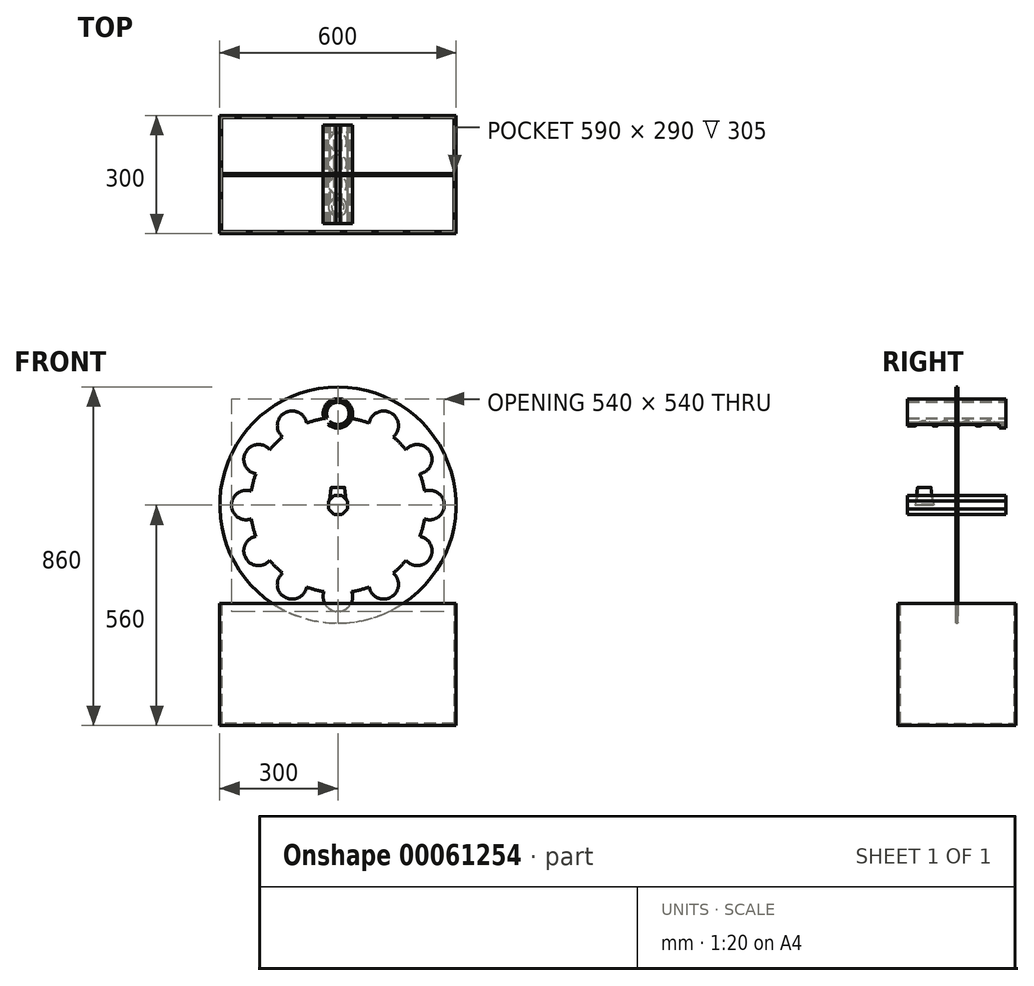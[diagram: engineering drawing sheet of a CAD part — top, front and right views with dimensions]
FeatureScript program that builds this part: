
annotation { "Feature Type Name" : "Feature", "Feature Type Description" : "" }
export const myFeature = defineFeature(function(context is Context, id is Id, definition is map)
    precondition{}
    {
        {
            assignVariable(context, id + "F0", {"name" : "depth", "anyValue" : 250});
        }
        {
            var Q0;
            Q0=qCreatedBy(makeId("Front.planeOp"),FACE);
            var sketch = newSketch(context, id + "F1", { "sketchPlane" : qUnion([Q0])});
            skLineSegment(sketch, "E0.rect.bottom", {"start": v(300, -250) * mm, "end": v(-300, -250) * mm});
            skLineSegment(sketch, "E0.rect.top", {"start": v(300, -560) * mm, "end": v(-300, -560) * mm});
            skLineSegment(sketch, "E0.rect.left", {"start": v(300, -250) * mm, "end": v(300, -560) * mm});
            skLineSegment(sketch, "E0.rect.right", {"start": v(-300, -250) * mm, "end": v(-300, -560) * mm});
            skPoint(sketch, "E0.rect.middle", {"position": v(0, -405) * mm});
            skSolve(sketch);
        }
        {
            var Q0;
            Q0 = qSketchRegion(id + "F1", true);
            extrude(context, id + "F2", {"entities" : qUnion([Q0]), "endBound" : BoundingType.SYMMETRIC, "depth" : 300 * mm});
        }
        {
            var Q0;
            Q0=makeQuery(id+"F2.opExtrude","SWEPT_FACE",FACE,{"disambiguationData":[OSD([sQuery(id+"F1.wireOp",EDGE,"E0.rect.bottom")])]});
            shell(context, id + "F3", {"entities" : qUnion([Q0]), "thickness" : 5 * mm});
        }
        {
            var Q0;
            Q0=qCreatedBy(makeId("Front.planeOp"),FACE);
            var sketch = newSketch(context, id + "F4", { "sketchPlane" : qUnion([Q0])});
            skCircle(sketch, "E1", {"center": v(0, 0) * mm, "radius": 300 * mm});
            skCircle(sketch, "E2", {"center": v(0, 0) * mm, "radius": 232.83 * mm, "construction": true});
            skArc(sketch, "E3", {"start": v(-5, 270) * mm, "mid": v(0, 195.33) * mm, "end": v(5, 270) * mm});
            skCircle(sketch, "E4", {"center": v(0, 232.83) * mm, "radius": 33.9 * mm});
            skCircle(sketch, "E5", {"center": v(0, 232.83) * mm, "radius": 31.5 * mm});
            skCircle(sketch, "E6", {"center": v(0, 232.83) * mm, "radius": 28.5 * mm});
            skCircle(sketch, "E7", {"center": v(0, 0) * mm, "radius": 222.83 * mm});
            skCircle(sketch, "E8.cCircle", {"center": v(0, 0) * mm, "radius": 24.14 * mm, "construction": true});
            skLineSegment(sketch, "E8.0", {"start": v(24.14, 10) * mm, "end": v(24.14, -10) * mm});
            skLineSegment(sketch, "E8.1", {"start": v(24.14, -10) * mm, "end": v(10, -24.14) * mm});
            skLineSegment(sketch, "E8.2", {"start": v(10, -24.14) * mm, "end": v(-10, -24.14) * mm});
            skLineSegment(sketch, "E8.3", {"start": v(-10, -24.14) * mm, "end": v(-24.14, -10) * mm});
            skLineSegment(sketch, "E8.4", {"start": v(-24.14, -10) * mm, "end": v(-24.14, 10) * mm});
            skLineSegment(sketch, "E8.5", {"start": v(-24.14, 10) * mm, "end": v(-10, 24.14) * mm});
            skLineSegment(sketch, "E8.6", {"start": v(-10, 24.14) * mm, "end": v(10, 24.14) * mm});
            skLineSegment(sketch, "E8.7", {"start": v(10, 24.14) * mm, "end": v(24.14, 10) * mm});
            skPoint(sketch, "E8.0.midPoint", {"position": v(24.14, 0) * mm});
            skLineSegment(sketch, "E9", {"start": v(0, 232.83) * mm, "end": v(-25, 204.88) * mm});
            skLineSegment(sketch, "E10", {"start": v(0, 232.83) * mm, "end": v(25, 204.88) * mm});
            skLineSegment(sketch, "E11", {"start": v(-25, 204.88) * mm, "end": v(25, 204.88) * mm, "construction": true});
            skLineSegment(sketch, "E12", {"start": v(-5, 270) * mm, "end": v(5, 270) * mm});
            skArc(sketch, "E13.1.0", {"start": v(-139.33, 231.33) * mm, "mid": v(-97.67, 169.16) * mm, "end": v(-130.67, 236.33) * mm});
            skLineSegment(sketch, "E13.1.1", {"start": v(-139.33, 231.33) * mm, "end": v(-130.67, 236.33) * mm});
            skArc(sketch, "E13.2.0", {"start": v(-236.33, 130.67) * mm, "mid": v(-169.16, 97.67) * mm, "end": v(-231.33, 139.33) * mm});
            skLineSegment(sketch, "E13.2.1", {"start": v(-236.33, 130.67) * mm, "end": v(-231.33, 139.33) * mm});
            skArc(sketch, "E14.1.3.0", {"start": v(-270, -5) * mm, "mid": v(-195.33, 0) * mm, "end": v(-270, 5) * mm});
            skLineSegment(sketch, "E14.4.3.0", {"start": v(-270, -5) * mm, "end": v(-270, 5) * mm});
            skArc(sketch, "E14.1.4.0", {"start": v(-231.33, -139.33) * mm, "mid": v(-169.16, -97.67) * mm, "end": v(-236.33, -130.67) * mm});
            skLineSegment(sketch, "E14.4.4.0", {"start": v(-231.33, -139.33) * mm, "end": v(-236.33, -130.67) * mm});
            skArc(sketch, "E14.1.5.0", {"start": v(-130.67, -236.33) * mm, "mid": v(-97.67, -169.16) * mm, "end": v(-139.33, -231.33) * mm});
            skLineSegment(sketch, "E14.4.5.0", {"start": v(-130.67, -236.33) * mm, "end": v(-139.33, -231.33) * mm});
            skArc(sketch, "E14.1.6.0", {"start": v(5, -270) * mm, "mid": v(0, -195.33) * mm, "end": v(-5, -270) * mm});
            skLineSegment(sketch, "E14.4.6.0", {"start": v(5, -270) * mm, "end": v(-5, -270) * mm});
            skArc(sketch, "E14.1.7.0", {"start": v(139.33, -231.33) * mm, "mid": v(97.67, -169.16) * mm, "end": v(130.67, -236.33) * mm});
            skLineSegment(sketch, "E14.4.7.0", {"start": v(139.33, -231.33) * mm, "end": v(130.67, -236.33) * mm});
            skArc(sketch, "E14.1.8.0", {"start": v(236.33, -130.67) * mm, "mid": v(169.16, -97.67) * mm, "end": v(231.33, -139.33) * mm});
            skLineSegment(sketch, "E14.4.8.0", {"start": v(236.33, -130.67) * mm, "end": v(231.33, -139.33) * mm});
            skArc(sketch, "E14.1.9.0", {"start": v(270, 5) * mm, "mid": v(195.33, 0) * mm, "end": v(270, -5) * mm});
            skLineSegment(sketch, "E14.4.9.0", {"start": v(270, 5) * mm, "end": v(270, -5) * mm});
            skArc(sketch, "E14.1.10.0", {"start": v(231.33, 139.33) * mm, "mid": v(169.16, 97.67) * mm, "end": v(236.33, 130.67) * mm});
            skLineSegment(sketch, "E14.4.10.0", {"start": v(231.33, 139.33) * mm, "end": v(236.33, 130.67) * mm});
            skArc(sketch, "E14.1.11.0", {"start": v(130.67, 236.33) * mm, "mid": v(97.67, 169.16) * mm, "end": v(139.33, 231.33) * mm});
            skLineSegment(sketch, "E14.4.11.0", {"start": v(130.67, 236.33) * mm, "end": v(139.33, 231.33) * mm});
            skSolve(sketch);
        }
        {
            var Q0;
            Q0=makeQuery(id+"F4.imprint","IMPRINT",FACE,{"disambiguationData":[TD([[makeQuery(id+"F4.imprint","IMPRINT",EDGE,{"derivedFrom":sQuery(id+"F4.wireOp",EDGE,"E1")}),1.0]])]});
            extrude(context, id + "F5", {"entities" : qUnion([Q0]), "endBound" : BoundingType.SYMMETRIC, "depth" : 5 * mm});
        }
        {
            var Q0;
            {var subQ0=sQuery(id+"F4.wireOp",EDGE,"E7");var subQ1=sQuery(id+"F4.wireOp",EDGE,"E3");var subQ2=makeQuery(id+"F4.imprint","INTERSECT",VERTEX,{"disambiguationData":[OD(0.0)],"derivedFrom":[subQ1,subQ0]});Q0=makeQuery(id+"F4.imprint","IMPRINT",FACE,{"disambiguationData":[TD([[makeQuery(id+"F4.imprint","IMPRINT",EDGE,{"disambiguationData":[TD([[subQ2,-1.0]])],"derivedFrom":subQ1}),1.0]])]});}
            var Q1;
            {var subQ0=sQuery(id+"F4.wireOp",EDGE,"E7");var subQ1=sQuery(id+"F4.wireOp",EDGE,"E3");var subQ2=makeQuery(id+"F4.imprint","INTERSECT",VERTEX,{"disambiguationData":[OD(0.0)],"derivedFrom":[subQ1,subQ0]});Q1=makeQuery(id+"F4.imprint","IMPRINT",FACE,{"disambiguationData":[TD([[makeQuery(id+"F4.imprint","IMPRINT",EDGE,{"disambiguationData":[TD([[subQ2,1.0]])],"derivedFrom":subQ1}),1.0]])]});}
            var Q2;
            {var subQ0=sQuery(id+"F4.wireOp",EDGE,"E10");var subQ1=sQuery(id+"F4.wireOp",EDGE,"E3");var subQ2=makeQuery(id+"F4.imprint","INTERSECT",VERTEX,{"derivedFrom":[subQ1,subQ0]});Q2=makeQuery(id+"F4.imprint","IMPRINT",FACE,{"disambiguationData":[TD([[makeQuery(id+"F4.imprint","IMPRINT",EDGE,{"disambiguationData":[TD([[subQ2,-1.0]])],"derivedFrom":subQ1}),1.0]])]});}
            var Q3;
            {var subQ0=sQuery(id+"F4.wireOp",EDGE,"E9");var subQ1=sQuery(id+"F4.wireOp",EDGE,"E3");var subQ2=makeQuery(id+"F4.imprint","INTERSECT",VERTEX,{"derivedFrom":[subQ1,subQ0]});Q3=makeQuery(id+"F4.imprint","IMPRINT",FACE,{"disambiguationData":[TD([[makeQuery(id+"F4.imprint","IMPRINT",EDGE,{"disambiguationData":[TD([[subQ2,-1.0]])],"derivedFrom":subQ1}),1.0]])]});}
            extrude(context, id + "F6", {"entities" : qUnion([Q0, Q1, Q2, Q3]), "endBound" : BoundingType.SYMMETRIC, "depth" : (getVariable(context, 'depth')) * mm});
        }
        {
            var Q0;
            {var subQ0=sQuery(id+"F4.wireOp",EDGE,"E9");var subQ1=sQuery(id+"F4.wireOp",EDGE,"E3");var subQ2=makeQuery(id+"F4.imprint","INTERSECT",VERTEX,{"derivedFrom":[subQ1,subQ0]});Q0=makeQuery(id+"F4.imprint","IMPRINT",FACE,{"disambiguationData":[TD([[makeQuery(id+"F4.imprint","IMPRINT",EDGE,{"disambiguationData":[TD([[subQ2,-1.0]])],"derivedFrom":subQ1}),1.0]])]});}
            extrude(context, id + "F7", {"entities" : qUnion([Q0]), "operationType" : NewBodyOperationType.REMOVE, "oppositeDirection" : true, "depth" : 107.9 * mm, "hasSecondDirection" : true, "secondDirectionBound" : SecondDirectionBoundingType.THROUGH_ALL, "secondDirectionOppositeDirection" : false, "secondDirectionDepth" : 25 * mm});
        }
        {
            var Q0;
            {var subQ0=sQuery(id+"F4.wireOp",EDGE,"E7");var subQ1=sQuery(id+"F4.wireOp",EDGE,"E5");var subQ2=makeQuery(id+"F4.imprint","INTERSECT",VERTEX,{"disambiguationData":[OD(0.0)],"derivedFrom":[subQ1,subQ0]});Q0=makeQuery(id+"F4.imprint","IMPRINT",FACE,{"disambiguationData":[TD([[makeQuery(id+"F4.imprint","IMPRINT",EDGE,{"disambiguationData":[TD([[subQ2,-1.0]])],"derivedFrom":subQ1}),1.0]])]});}
            var Q1;
            {var subQ0=sQuery(id+"F4.wireOp",EDGE,"E7");var subQ1=sQuery(id+"F4.wireOp",EDGE,"E5");var subQ2=makeQuery(id+"F4.imprint","INTERSECT",VERTEX,{"disambiguationData":[OD(0.0)],"derivedFrom":[subQ1,subQ0]});Q1=makeQuery(id+"F4.imprint","IMPRINT",FACE,{"disambiguationData":[TD([[makeQuery(id+"F4.imprint","IMPRINT",EDGE,{"disambiguationData":[TD([[subQ2,1.0]])],"derivedFrom":subQ1}),1.0]])]});}
            var Q2;
            {var subQ0=sQuery(id+"F4.wireOp",EDGE,"E10");var subQ1=sQuery(id+"F4.wireOp",EDGE,"E5");var subQ2=makeQuery(id+"F4.imprint","INTERSECT",VERTEX,{"derivedFrom":[subQ1,subQ0]});Q2=makeQuery(id+"F4.imprint","IMPRINT",FACE,{"disambiguationData":[TD([[makeQuery(id+"F4.imprint","IMPRINT",EDGE,{"disambiguationData":[TD([[subQ2,-1.0]])],"derivedFrom":subQ1}),1.0]])]});}
            var Q3;
            {var subQ0=sQuery(id+"F4.wireOp",EDGE,"E9");var subQ1=sQuery(id+"F4.wireOp",EDGE,"E5");var subQ2=makeQuery(id+"F4.imprint","INTERSECT",VERTEX,{"derivedFrom":[subQ1,subQ0]});Q3=makeQuery(id+"F4.imprint","IMPRINT",FACE,{"disambiguationData":[TD([[makeQuery(id+"F4.imprint","IMPRINT",EDGE,{"disambiguationData":[TD([[subQ2,-1.0]])],"derivedFrom":subQ1}),1.0]])]});}
            extrude(context, id + "F8", {"entities" : qUnion([Q0, Q1, Q2, Q3]), "endBound" : BoundingType.SYMMETRIC, "depth" : (getVariable(context, 'depth')) * mm});
        }
        {
            var Q0;
            Q0=qCreatedBy(makeId("Top.planeOp"),FACE);
            var sketch = newSketch(context, id + "F9", { "sketchPlane" : qUnion([Q0])});
            skCircle(sketch, "E15", {"center": v(0, -82.5) * mm, "radius": 22.5 * mm});
            skLineSegment(sketch, "E16", {"start": v(0, -82.5) * mm, "end": v(0, 82.5) * mm, "construction": true});
            skCircle(sketch, "E17", {"center": v(0, 82.5) * mm, "radius": 22.5 * mm});
            skCircle(sketch, "E18", {"center": v(0, 27.5) * mm, "radius": 22.5 * mm});
            skCircle(sketch, "E19", {"center": v(0, -27.5) * mm, "radius": 22.5 * mm});
            skLineSegment(sketch, "E20", {"start": v(0, -27.5) * mm, "end": v(0, 27.5) * mm, "construction": true});
            skLineSegment(sketch, "E21", {"start": v(0, 82.5) * mm, "end": v(0, 27.5) * mm, "construction": true});
            skSolve(sketch);
        }
        {
            var Q0;
            Q0 = qSketchRegion(id + "F9", true);
            var Q1;
            Q1=makeQuery(id+"F8.opExtrude","SWEPT_FACE",FACE,{"disambiguationData":[OSD([sQuery(id+"F4.wireOp",EDGE,"E6")])]});
            var Q2;
            Q2=makeQuery(id+"F8.opExtrude","SWEPT_BODY",BODY,{"disambiguationData":[OSD([sQuery(id+"F4.wireOp",EDGE,"E5"),sQuery(id+"F4.wireOp",EDGE,"E6")])]});
            extrude(context, id + "F10", {"entities" : qUnion([Q0]), "operationType" : NewBodyOperationType.REMOVE, "endBound" : BoundingType.UP_TO_SURFACE, "endBoundEntityFace" : qUnion([Q1]), "endBoundEntityBody" : qUnion([Q2]), "depth" : 226.12 * mm});
        }
        {
            var Q0;
            Q0=makeQuery(id+"F4.imprint","IMPRINT",FACE,{"disambiguationData":[TD([[makeQuery(id+"F4.imprint","IMPRINT",EDGE,{"derivedFrom":sQuery(id+"F4.wireOp",EDGE,"E8.0")}),-1.0]])]});
            extrude(context, id + "F11", {"entities" : qUnion([Q0]), "endBound" : BoundingType.SYMMETRIC, "depth" : (getVariable(context, 'depth')) * mm});
        }
        {
            var Q0;
            Q0=qCreatedBy(makeId("Right.planeOp"),FACE);
            var sketch = newSketch(context, id + "F12", { "sketchPlane" : qUnion([Q0])});
            skLineSegment(sketch, "E22.0", {"start": v(-105, 0) * mm, "end": v(-60, 0) * mm, "construction": true});
            skLineSegment(sketch, "E23", {"start": v(-82.5, 43) * mm, "end": v(-82.5, 45) * mm});
            skLineSegment(sketch, "E24", {"start": v(-82.5, 45) * mm, "end": v(-99.72, 45) * mm});
            skLineSegment(sketch, "E25", {"start": v(-99.72, 45) * mm, "end": v(-105, 2) * mm});
            skLineSegment(sketch, "E26", {"start": v(-105, 2) * mm, "end": v(-106.43, 2) * mm});
            skLineSegment(sketch, "E27", {"start": v(-106.43, 2) * mm, "end": v(-106.43, 0) * mm});
            skLineSegment(sketch, "E28", {"start": v(-106.43, 0) * mm, "end": v(-105, 0) * mm});
            skLineSegment(sketch, "E29", {"start": v(-105, 0) * mm, "end": v(-103.43, 0) * mm});
            skLineSegment(sketch, "E30", {"start": v(-103.43, 0) * mm, "end": v(-98.15, 43) * mm});
            skLineSegment(sketch, "E31", {"start": v(-98.15, 43) * mm, "end": v(-82.5, 43) * mm});
            skPoint(sketch, "E32.orphan", {"position": v(-82.5, 0) * mm});
            skSolve(sketch);
        }
        {
            var Q0;
            Q0 = qSketchRegion(id + "F12", true);
            var Q1;
            Q1=sQuery(id+"F12.wireOp",EDGE,"E23");
            revolve(context, id + "F13", {"entities" : qUnion([Q0]), "axis" : qUnion([Q1]), "revolveType" : RevolveType.FULL});
        }
        {
            var Q0;
            Q0=makeQuery(id+"F13.opRevolve","SWEPT_EDGE",EDGE,{"disambiguationData":[OSD([sQuery(id+"F12.wireOp",EDGE,"E26"),sQuery(id+"F12.wireOp",EDGE,"E27")])]});
            var Q1;
            Q1=makeQuery(id+"F13.opRevolve","SWEPT_EDGE",EDGE,{"disambiguationData":[OSD([sQuery(id+"F12.wireOp",EDGE,"E29"),sQuery(id+"F12.wireOp",EDGE,"E30")])]});
            var Q2;
            Q2=makeQuery(id+"F13.opRevolve","SWEPT_EDGE",EDGE,{"disambiguationData":[OSD([sQuery(id+"F12.wireOp",EDGE,"E27"),sQuery(id+"F12.wireOp",EDGE,"E28")])]});
            var Q3;
            Q3=makeQuery(id+"F13.opRevolve","SWEPT_EDGE",EDGE,{"disambiguationData":[OSD([sQuery(id+"F12.wireOp",EDGE,"E25"),sQuery(id+"F12.wireOp",EDGE,"E26")])]});
            var Q4;
            Q4=makeQuery(id+"F13.opRevolve","SWEPT_EDGE",EDGE,{"disambiguationData":[OSD([sQuery(id+"F12.wireOp",EDGE,"E24"),sQuery(id+"F12.wireOp",EDGE,"E25")])]});
            fillet(context, id + "F14", {"entities" : qUnion([Q0, Q1, Q2, Q3, Q4]), "radius" : 0.4 * mm, "tangentPropagation" : true, "allowEdgeOverflow" : false});
        }
    });
